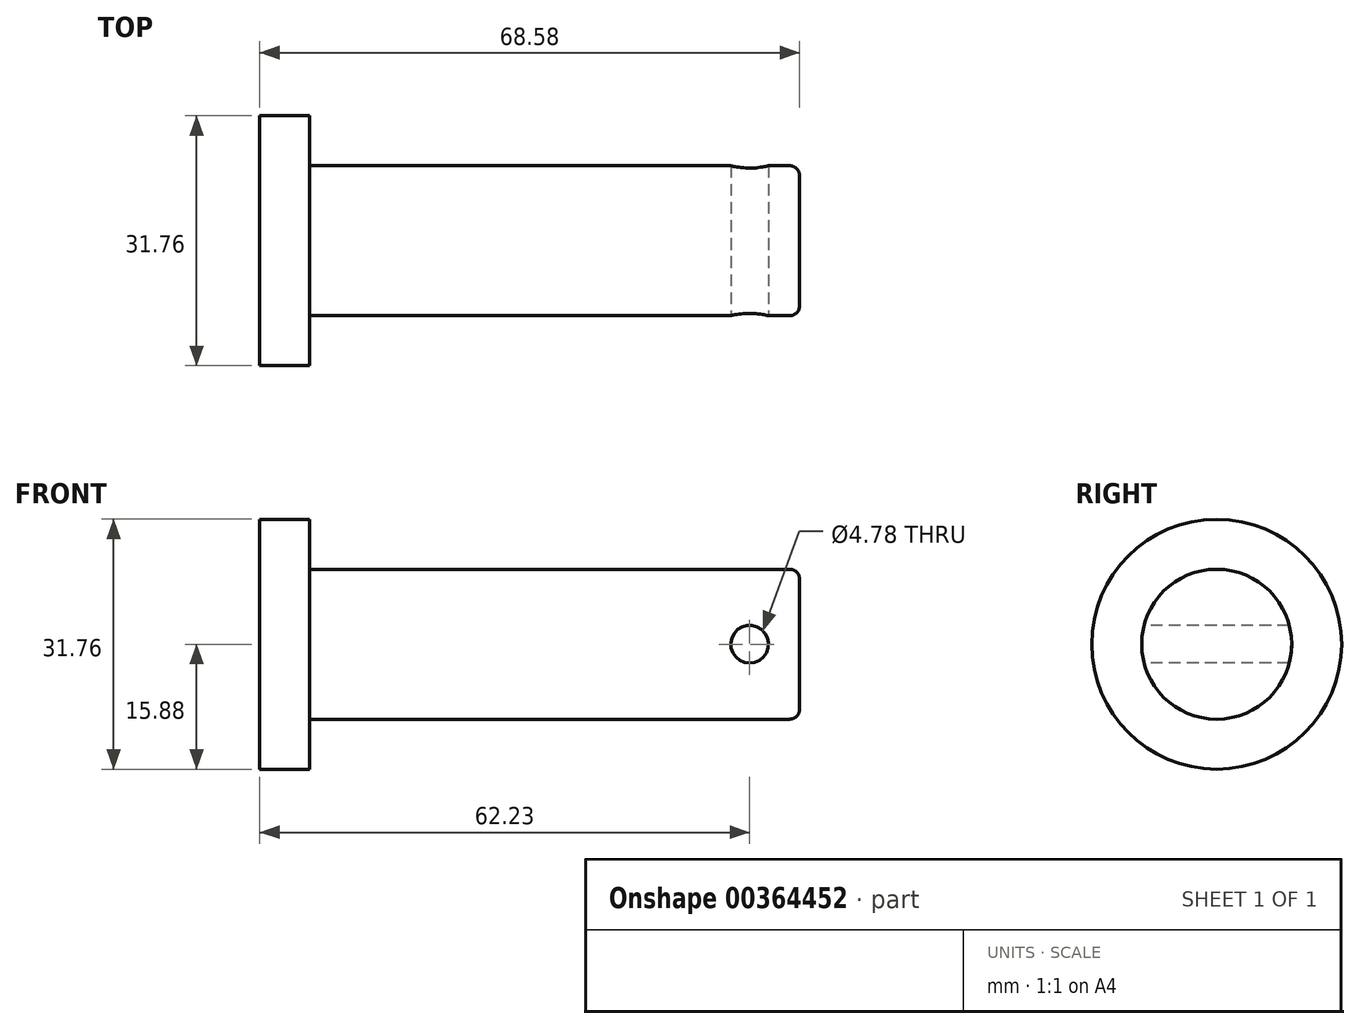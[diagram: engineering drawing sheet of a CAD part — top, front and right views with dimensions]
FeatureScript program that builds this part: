
annotation { "Feature Type Name" : "Feature", "Feature Type Description" : "" }
export const myFeature = defineFeature(function(context is Context, id is Id, definition is map)
    precondition{}
    {
        {
            var Q0;
            Q0=qCreatedBy(makeId("Right.planeOp"),FACE);
            var sketch = newSketch(context, id + "F0", { "sketchPlane" : qUnion([Q0])});
            skCircle(sketch, "E0", {"center": v(0, 0) * mm, "radius": 15.88 * mm});
            skCircle(sketch, "E1", {"center": v(0, 0) * mm, "radius": 9.53 * mm});
            skSolve(sketch);
        }
        {
            var Q0;
            Q0=makeQuery(id+"F0.imprint","IMPRINT",FACE,{"disambiguationData":[TD([[makeQuery(id+"F0.imprint","IMPRINT",EDGE,{"derivedFrom":sQuery(id+"F0.wireOp",EDGE,"E0")}),1.0]])]});
            extrude(context, id + "F1", {"entities" : qUnion([Q0]), "depth" : 6.35 * mm});
        }
        {
            var Q0;
            Q0=makeQuery(id+"F0.imprint","IMPRINT",FACE,{"disambiguationData":[TD([[makeQuery(id+"F0.imprint","IMPRINT",EDGE,{"derivedFrom":sQuery(id+"F0.wireOp",EDGE,"E1")}),1.0]])]});
            extrude(context, id + "F2", {"entities" : qUnion([Q0]), "operationType" : NewBodyOperationType.ADD, "depth" : 68.58 * mm});
        }
        {
            var Q0;
            Q0=qCreatedBy(makeId("Front.planeOp"),FACE);
            var sketch = newSketch(context, id + "F3", { "sketchPlane" : qUnion([Q0])});
            skLineSegment(sketch, "E2", {"start": v(6.35, 9.53) * mm, "end": v(62.23, 9.53) * mm});
            skLineSegment(sketch, "E3", {"start": v(62.23, -9.53) * mm, "end": v(6.35, -9.53) * mm});
            skCircle(sketch, "E4", {"center": v(62.23, 0) * mm, "radius": 2.39 * mm});
            skSolve(sketch);
        }
        {
            var Q0;
            Q0 = qSketchRegion(id + "F3", true);
            extrude(context, id + "F4", {"entities" : qUnion([Q0]), "operationType" : NewBodyOperationType.REMOVE, "endBound" : BoundingType.THROUGH_ALL, "oppositeDirection" : true, "depth" : 25.4 * mm, "hasSecondDirection" : true, "secondDirectionOppositeDirection" : false, "secondDirectionDepth" : 25.4 * mm});
        }
        {
            var Q0;
            Q0=makeQuery(id+"F2.opExtrude","CAP_EDGE",EDGE,{"disambiguationData":[OSD([sQuery(id+"F0.wireOp",EDGE,"E1")])],"isStart":false});
            fillet(context, id + "F5", {"entities" : qUnion([Q0]), "radius" : 1.27 * mm, "tangentPropagation" : true, "allowEdgeOverflow" : false});
        }
    });
